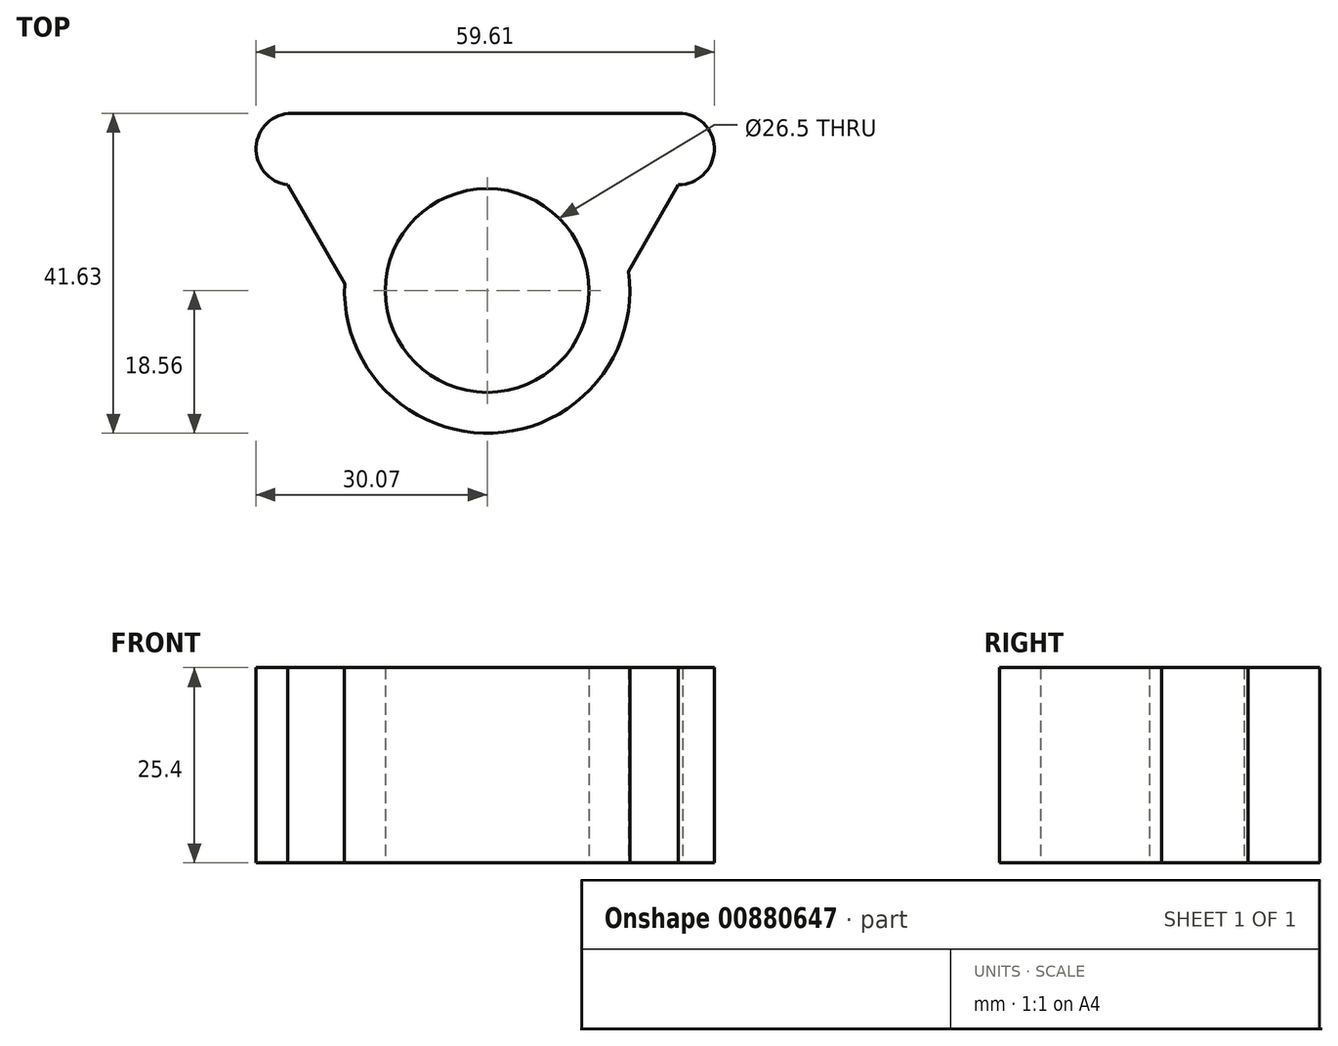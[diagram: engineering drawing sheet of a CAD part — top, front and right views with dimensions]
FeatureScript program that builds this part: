
annotation { "Feature Type Name" : "Feature", "Feature Type Description" : "" }
export const myFeature = defineFeature(function(context is Context, id is Id, definition is map)
    precondition{}
    {
        {
            var Q0;
            Q0=qCreatedBy(makeId("Top.planeOp"),FACE);
            var sketch = newSketch(context, id + "F0", { "sketchPlane" : qUnion([Q0])});
            skCircle(sketch, "E0", {"center": v(0, 0) * mm, "radius": 13.25 * mm});
            skCircle(sketch, "E1", {"center": v(0, 0) * mm, "radius": 18.56 * mm});
            skSolve(sketch);
        }
        {
            var Q0;
            Q0=makeQuery(id+"F0.imprint","IMPRINT",FACE,{"disambiguationData":[TD([[makeQuery(id+"F0.imprint","IMPRINT",EDGE,{"derivedFrom":sQuery(id+"F0.wireOp",EDGE,"E0")}),-1.0]])]});
            extrude(context, id + "F1", {"entities" : qUnion([Q0]), "depth" : 25.4 * mm, "offsetDistance" : 25.4 * mm});
        }
        {
            var Q0;
            Q0=qCreatedBy(makeId("Top.planeOp"),FACE);
            var sketch = newSketch(context, id + "F2", { "sketchPlane" : qUnion([Q0])});
            skLineSegment(sketch, "E2", {"start": v(0, 16.38) * mm, "end": v(0, 23.07) * mm});
            skLineSegment(sketch, "E3", {"start": v(0, 23.07) * mm, "end": v(-25.4, 23.07) * mm});
            skLineSegment(sketch, "E4", {"start": v(0, 23.07) * mm, "end": v(25.4, 23.07) * mm});
            skArc(sketch, "E5", {"start": v(-25.4, 23.07) * mm, "mid": v(-30.06, 18.67) * mm, "end": v(-25.93, 13.77) * mm});
            skLineSegment(sketch, "E6", {"start": v(-25.93, 13.77) * mm, "end": v(24.87, 13.77) * mm});
            skArc(sketch, "E7", {"start": v(24.87, 13.77) * mm, "mid": v(29.53, 18.17) * mm, "end": v(25.4, 23.07) * mm});
            skLineSegment(sketch, "E8", {"start": v(-25.93, 13.77) * mm, "end": v(-18.03, 0) * mm});
            skLineSegment(sketch, "E9", {"start": v(-18.03, 0) * mm, "end": v(-9.2, 13.77) * mm});
            skLineSegment(sketch, "E10", {"start": v(-9.2, 13.77) * mm, "end": v(24.87, 13.77) * mm});
            skLineSegment(sketch, "E11", {"start": v(24.87, 13.77) * mm, "end": v(16.96, 0) * mm});
            skLineSegment(sketch, "E12", {"start": v(16.96, 0) * mm, "end": v(7.83, 13.77) * mm});
            skSolve(sketch);
        }
        {
            var Q0;
            Q0=makeQuery(id+"F2.imprint","IMPRINT",FACE,{"disambiguationData":[TD([[makeQuery(id+"F2.imprint","IMPRINT",EDGE,{"derivedFrom":sQuery(id+"F2.wireOp",EDGE,"E6")}),-1.0]])]});
            var Q1;
            Q1=makeQuery(id+"F2.imprint","IMPRINT",FACE,{"disambiguationData":[TD([[makeQuery(id+"F2.imprint","IMPRINT",EDGE,{"derivedFrom":sQuery(id+"F2.wireOp",EDGE,"E3")}),1.0]])]});
            var Q2;
            {var subQ0=sQuery(id+"F2.wireOp",EDGE,"E11");Q2=makeQuery(id+"F2.imprint","IMPRINT",FACE,{"disambiguationData":[TD([[makeQuery(id+"F2.imprint","IMPRINT",EDGE,{"derivedFrom":subQ0}),-1.0]])]});}
            extrude(context, id + "F3", {"entities" : qUnion([Q0, Q1, Q2]), "operationType" : NewBodyOperationType.ADD, "depth" : 25.4 * mm, "offsetDistance" : 25.4 * mm});
        }
    });
